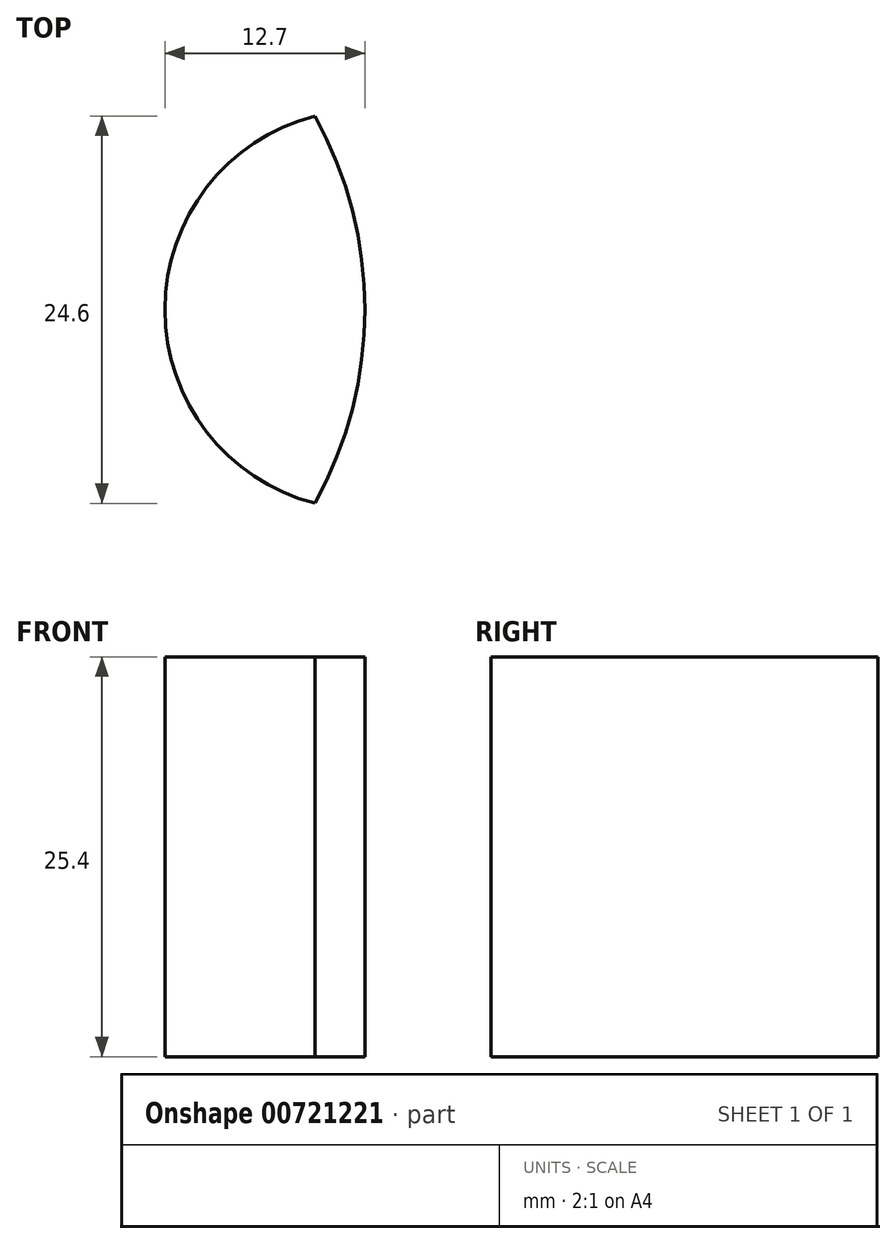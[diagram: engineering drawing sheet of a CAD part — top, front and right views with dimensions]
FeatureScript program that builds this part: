
annotation { "Feature Type Name" : "Feature", "Feature Type Description" : "" }
export const myFeature = defineFeature(function(context is Context, id is Id, definition is map)
    precondition{}
    {
        {
            var Q0;
            Q0=qCreatedBy(makeId("Top.planeOp"),FACE);
            var sketch = newSketch(context, id + "F0", { "sketchPlane" : qUnion([Q0])});
            skCircle(sketch, "E0", {"center": v(0, 0) * mm, "radius": 25.4 * mm});
            skCircle(sketch, "E1", {"center": v(25.4, 0) * mm, "radius": 12.7 * mm});
            skSolve(sketch);
        }
        {
            var Q0;
            {var subQ0=sQuery(id+"F0.wireOp",EDGE,"E1");var subQ1=sQuery(id+"F0.wireOp",EDGE,"E0");var subQ2=makeQuery(id+"F0.imprint","INTERSECT",VERTEX,{"disambiguationData":[OD(0.0)],"derivedFrom":[subQ1,subQ0]});Q0=makeQuery(id+"F0.imprint","IMPRINT",FACE,{"disambiguationData":[TD([[makeQuery(id+"F0.imprint","IMPRINT",EDGE,{"disambiguationData":[TD([[subQ2,1.0]])],"derivedFrom":subQ1}),1.0]])]});}
            var Q1;
            {var subQ0=sQuery(id+"F0.wireOp",EDGE,"E1");var subQ1=sQuery(id+"F0.wireOp",EDGE,"E0");var subQ2=makeQuery(id+"F0.imprint","INTERSECT",VERTEX,{"disambiguationData":[OD(0.0)],"derivedFrom":[subQ1,subQ0]});Q1=makeQuery(id+"F0.imprint","IMPRINT",FACE,{"disambiguationData":[TD([[makeQuery(id+"F0.imprint","IMPRINT",EDGE,{"disambiguationData":[TD([[subQ2,-1.0]])],"derivedFrom":subQ1}),1.0]])]});}
            extrude(context, id + "F1", {"entities" : qUnion([Q0, Q1]), "depth" : 25.4 * mm, "offsetDistance" : 25.4 * mm});
        }
        {
            var Q0;
            {var subQ0=sQuery(id+"F0.wireOp",EDGE,"E1");var subQ1=sQuery(id+"F0.wireOp",EDGE,"E0");var subQ2=makeQuery(id+"F0.imprint","INTERSECT",VERTEX,{"disambiguationData":[OD(0.0)],"derivedFrom":[subQ1,subQ0]});Q0=makeQuery(id+"F0.imprint","IMPRINT",FACE,{"disambiguationData":[TD([[makeQuery(id+"F0.imprint","IMPRINT",EDGE,{"disambiguationData":[TD([[subQ2,-1.0]])],"derivedFrom":subQ1}),-1.0]])]});}
            var Q1;
            {var subQ0=sQuery(id+"F0.wireOp",EDGE,"E1");var subQ1=sQuery(id+"F0.wireOp",EDGE,"E0");var subQ2=makeQuery(id+"F0.imprint","INTERSECT",VERTEX,{"disambiguationData":[OD(0.0)],"derivedFrom":[subQ1,subQ0]});Q1=makeQuery(id+"F0.imprint","IMPRINT",FACE,{"disambiguationData":[TD([[makeQuery(id+"F0.imprint","IMPRINT",EDGE,{"disambiguationData":[TD([[subQ2,-1.0]])],"derivedFrom":subQ1}),1.0]])]});}
            extrude(context, id + "F2", {"entities" : qUnion([Q0, Q1]), "depth" : 25.4 * mm, "offsetDistance" : 25.4 * mm});
        }
        {
            var Q0;
            Q0=makeQuery(id+"F2.opExtrude","SWEPT_BODY",BODY,{"disambiguationData":[OSD([sQuery(id+"F0.wireOp",EDGE,"E1")])]});
            var Q1;
            Q1=makeQuery(id+"F1.opExtrude","SWEPT_BODY",BODY,{"disambiguationData":[OSD([sQuery(id+"F0.wireOp",EDGE,"E0")])]});
            var Q2;
            Q2=makeQuery(id+"F1.opExtrude","SWEPT_BODY",BODY,{"disambiguationData":[OSD([sQuery(id+"F0.wireOp",EDGE,"E0")])]});
            booleanBodies(context, id + "F3", {"operationType" : BooleanOperationType.INTERSECTION, "tools" : qUnion([Q0, Q1]), "targets" : qUnion([Q2])});
        }
    });
